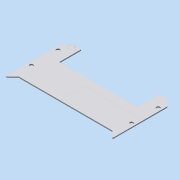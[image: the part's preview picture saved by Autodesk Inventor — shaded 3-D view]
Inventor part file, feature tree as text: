
AUTODESK INVENTOR PART (.ipt)
format: ipt  version: 2015 (Build 190159000, 159)  size: 442,880 bytes
history: native  units: in
note: dims shown in document units (in); Inventor stores cm internally (conversion verified against a paired STEP export)
features: other x4, extrude x1, fillet x1, sketch x1, projected_geometry x1
ambient origin geometry x8: Origin, YZ Plane, XZ Plane, XY Plane, X Axis, Y Axis, Z Axis, Center Point
bodies: Solid1 (feature_tree)
feature tree (8):
  other  "BatteryEnclosure.ipt"
  extrude  "Extrusion1"  Depth=0.0625in TaperAngle=0.0deg
  fillet  "Fillet1"  Radius=0.0312in
  other  "TaggingFeature1"
  sketch  "Sketch1"  dims[d0=0.3937in d2=0.0625in d3=0.0in d4=0.0312in d5=0.0312in d6=0.0312in d8=1.25in]
  other  "Solid2::BatteryEnclosure.ipt"
  other  "Srf1"
  projected_geometry  "Project Cut Edges1"
